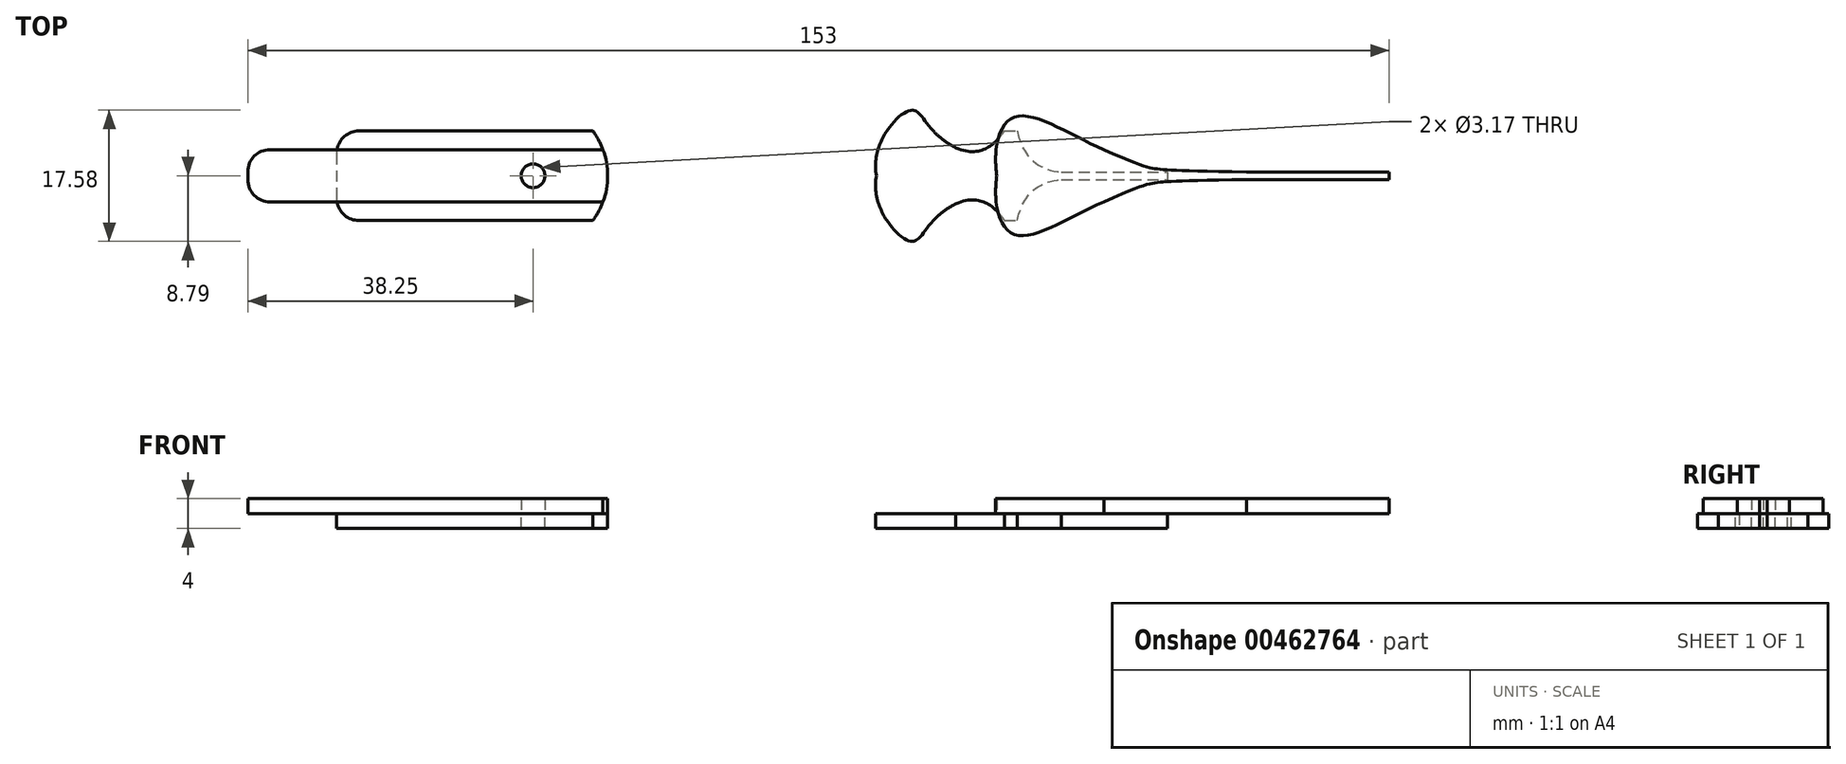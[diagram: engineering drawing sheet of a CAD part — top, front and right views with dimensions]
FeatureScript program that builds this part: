
annotation { "Feature Type Name" : "Feature", "Feature Type Description" : "" }
export const myFeature = defineFeature(function(context is Context, id is Id, definition is map)
    precondition{}
    {
        {
            var Q0;
            Q0=qCreatedBy(makeId("Top.planeOp"),FACE);
            var sketch = newSketch(context, id + "F0", { "sketchPlane" : qUnion([Q0])});
            skCircle(sketch, "E0", {"center": v(0, 0) * mm, "radius": 1.59 * mm});
            skLineSegment(sketch, "E1.bottom", {"start": v(-38.25, 3.5) * mm, "end": v(114.75, 3.5) * mm});
            skLineSegment(sketch, "E1.top", {"start": v(-38.25, -3.5) * mm, "end": v(114.75, -3.5) * mm});
            skLineSegment(sketch, "E1.left", {"start": v(-38.25, 3.5) * mm, "end": v(-38.25, -3.5) * mm});
            skLineSegment(sketch, "E1.right", {"start": v(114.75, 3.5) * mm, "end": v(114.75, -3.5) * mm});
            skCircle(sketch, "E2", {"center": v(0, 0) * mm, "radius": 10 * mm});
            skFitSpline(sketch, "E3", {"points": [v(76.5, -3.5) * mm, v(83.35, -0.96) * mm, v(95.63, -0.5) * mm], "startDerivative": vector(32.58, 14.52) * mm, "endDerivative": vector(48.68, 0.82) * mm});
            skFitSpline(sketch, "E4", {"points": [v(76.5, -3.5) * mm, v(64.47, -7.85) * mm, v(62.16, 0) * mm], "startDerivative": vector(-24.35, -10.45) * mm, "endDerivative": vector(3.38, 23.63) * mm});
            skLineSegment(sketch, "E5", {"start": v(0, 0) * mm, "end": v(229.5, 0) * mm, "construction": true});
            skLineSegment(sketch, "E6", {"start": v(95.63, -0.5) * mm, "end": v(114.75, -0.5) * mm});
            skFitSpline(sketch, "E7.MirrorCS", {"points": [v(76.5, 3.5) * mm, v(64.47, 7.85) * mm, v(62.16, 0) * mm], "startDerivative": vector(-24.35, 10.45) * mm, "endDerivative": vector(3.38, -23.63) * mm});
            skFitSpline(sketch, "E8.MirrorCS", {"points": [v(76.5, 3.5) * mm, v(83.35, 0.96) * mm, v(95.63, 0.5) * mm], "startDerivative": vector(32.58, -14.52) * mm, "endDerivative": vector(48.68, -0.82) * mm});
            skLineSegment(sketch, "E9.MirrorCS", {"start": v(95.63, 0.5) * mm, "end": v(114.75, 0.5) * mm});
            skSolve(sketch);
        }
        {
            var Q0;
            {var subQ0=sQuery(id+"F0.wireOp",EDGE,"E1.left");Q0=makeQuery(id+"F0.imprint","IMPRINT",FACE,{"disambiguationData":[TD([[makeQuery(id+"F0.imprint","IMPRINT",EDGE,{"derivedFrom":subQ0}),1.0]])]});}
            var Q1;
            {var subQ0=sQuery(id+"F0.wireOp",EDGE,"E2");var subQ1=sQuery(id+"F0.wireOp",EDGE,"E1.bottom");var subQ2=makeQuery(id+"F0.imprint","INTERSECT",VERTEX,{"disambiguationData":[OD(0.0)],"derivedFrom":[subQ1,subQ0]});Q1=makeQuery(id+"F0.imprint","IMPRINT",FACE,{"disambiguationData":[TD([[makeQuery(id+"F0.imprint","IMPRINT",EDGE,{"disambiguationData":[TD([[subQ2,-1.0]])],"derivedFrom":subQ1}),1.0]])]});}
            var Q2;
            {var subQ0=sQuery(id+"F0.wireOp",EDGE,"E7.MirrorCS");var subQ1=sQuery(id+"F0.wireOp",EDGE,"E1.bottom");var subQ3=makeQuery(id+"F0.imprint","INTERSECT",VERTEX,{"derivedFrom":[subQ1,subQ0]});Q2=makeQuery(id+"F0.imprint","IMPRINT",FACE,{"disambiguationData":[TD([[makeQuery(id+"F0.imprint","IMPRINT",EDGE,{"disambiguationData":[TD([[subQ3,-1.0]])],"derivedFrom":subQ1}),1.0]])]});}
            var Q3;
            {var subQ0=sQuery(id+"F0.wireOp",EDGE,"E2");var subQ1=sQuery(id+"F0.wireOp",EDGE,"E1.top");var subQ2=makeQuery(id+"F0.imprint","INTERSECT",VERTEX,{"disambiguationData":[OD(0.0)],"derivedFrom":[subQ1,subQ0]});Q3=makeQuery(id+"F0.imprint","IMPRINT",FACE,{"disambiguationData":[TD([[makeQuery(id+"F0.imprint","IMPRINT",EDGE,{"disambiguationData":[TD([[subQ2,-1.0]])],"derivedFrom":subQ1}),-1.0]])]});}
            var Q4;
            {var subQ0=sQuery(id+"F0.wireOp",EDGE,"E4");var subQ1=sQuery(id+"F0.wireOp",EDGE,"E1.top");var subQ3=makeQuery(id+"F0.imprint","INTERSECT",VERTEX,{"derivedFrom":[subQ1,subQ0]});Q4=makeQuery(id+"F0.imprint","IMPRINT",FACE,{"disambiguationData":[TD([[makeQuery(id+"F0.imprint","IMPRINT",EDGE,{"disambiguationData":[TD([[subQ3,-1.0]])],"derivedFrom":subQ1}),-1.0]])]});}
            var Q5;
            {var subQ5=sQuery(id+"F0.wireOp",EDGE,"E2");var subQ6=sQuery(id+"F0.wireOp",EDGE,"E1.bottom");var subQ7=makeQuery(id+"F0.imprint","INTERSECT",VERTEX,{"disambiguationData":[OD(1.0)],"derivedFrom":[subQ6,subQ5]});Q5=makeQuery(id+"F0.imprint","IMPRINT",FACE,{"disambiguationData":[TD([[makeQuery(id+"F0.imprint","IMPRINT",EDGE,{"disambiguationData":[TD([[subQ7,-1.0]])],"derivedFrom":subQ6}),-1.0]])]});}
            var Q6;
            Q6=makeQuery(id+"F0.imprint","IMPRINT",FACE,{"disambiguationData":[TD([[makeQuery(id+"F0.imprint","IMPRINT",EDGE,{"derivedFrom":sQuery(id+"F0.wireOp",EDGE,"E0")}),-1.0]])]});
            var Q7;
            {var subQ8=sQuery(id+"F0.wireOp",EDGE,"E3");Q7=makeQuery(id+"F0.imprint","IMPRINT",FACE,{"disambiguationData":[TD([[makeQuery(id+"F0.imprint","IMPRINT",EDGE,{"derivedFrom":subQ8}),1.0]])]});}
            extrude(context, id + "F1", {"entities" : qUnion([Q0, Q1, Q2, Q3, Q4, Q5, Q6, Q7]), "depth" : 2 * mm});
        }
        {
            var Q0;
            Q0=qCreatedBy(makeId("Top.planeOp"),FACE);
            var sketch = newSketch(context, id + "F2", { "sketchPlane" : qUnion([Q0])});
            skCircle(sketch, "E10", {"center": v(0, 0) * mm, "radius": 1.59 * mm});
            skLineSegment(sketch, "E11.bottom", {"start": v(-26.33, 6) * mm, "end": v(85, 6) * mm});
            skLineSegment(sketch, "E11.top", {"start": v(-26.33, -6) * mm, "end": v(85, -6) * mm});
            skLineSegment(sketch, "E11.left", {"start": v(-26.33, 6) * mm, "end": v(-26.33, -6) * mm});
            skLineSegment(sketch, "E11.right", {"start": v(85, 6) * mm, "end": v(85, -6) * mm});
            skCircle(sketch, "E12", {"center": v(0, 0) * mm, "radius": 10 * mm});
            skLineSegment(sketch, "E13.right", {"start": v(85, -12.54) * mm, "end": v(85, -19.22) * mm});
            skFitSpline(sketch, "E14", {"points": [v(56.67, -3.75) * mm, v(64.42, -7.88) * mm, v(70.83, -0.5) * mm], "startDerivative": vector(32.58, 14.52) * mm, "endDerivative": vector(38.81, 3.07) * mm});
            skFitSpline(sketch, "E15", {"points": [v(56.67, -3.75) * mm, v(50.67, -8.78) * mm, v(46.04, 0) * mm], "startDerivative": vector(-26.59, -13.5) * mm, "endDerivative": vector(5.2, 23.3) * mm});
            skLineSegment(sketch, "E16", {"start": v(0, 0) * mm, "end": v(229.5, 0) * mm, "construction": true});
            skLineSegment(sketch, "E17", {"start": v(70.83, -0.5) * mm, "end": v(85, -0.5) * mm});
            skFitSpline(sketch, "E18.MirrorCS", {"points": [v(56.67, 3.75) * mm, v(50.67, 8.78) * mm, v(46.04, 0) * mm], "startDerivative": vector(-26.59, 13.5) * mm, "endDerivative": vector(5.2, -23.3) * mm});
            skFitSpline(sketch, "E19.MirrorCS", {"points": [v(56.67, 3.75) * mm, v(64.42, 7.88) * mm, v(70.83, 0.5) * mm], "startDerivative": vector(32.58, -14.52) * mm, "endDerivative": vector(38.81, -3.07) * mm});
            skLineSegment(sketch, "E20.MirrorCS", {"start": v(70.83, 0.5) * mm, "end": v(85, 0.5) * mm});
            skSolve(sketch);
        }
        {
            var Q0;
            {var subQ0=sQuery(id+"F2.wireOp",EDGE,"E11.left");Q0=makeQuery(id+"F2.imprint","IMPRINT",FACE,{"disambiguationData":[TD([[makeQuery(id+"F2.imprint","IMPRINT",EDGE,{"derivedFrom":subQ0}),1.0]])]});}
            var Q1;
            {var subQ0=sQuery(id+"F2.wireOp",EDGE,"E12");var subQ1=sQuery(id+"F2.wireOp",EDGE,"E11.bottom");var subQ2=makeQuery(id+"F2.imprint","INTERSECT",VERTEX,{"disambiguationData":[OD(0.0)],"derivedFrom":[subQ1,subQ0]});Q1=makeQuery(id+"F2.imprint","IMPRINT",FACE,{"disambiguationData":[TD([[makeQuery(id+"F2.imprint","IMPRINT",EDGE,{"disambiguationData":[TD([[subQ2,-1.0]])],"derivedFrom":subQ1}),1.0]])]});}
            var Q2;
            {var subQ0=sQuery(id+"F2.wireOp",EDGE,"E12");var subQ1=sQuery(id+"F2.wireOp",EDGE,"E11.top");var subQ2=makeQuery(id+"F2.imprint","INTERSECT",VERTEX,{"disambiguationData":[OD(0.0)],"derivedFrom":[subQ1,subQ0]});Q2=makeQuery(id+"F2.imprint","IMPRINT",FACE,{"disambiguationData":[TD([[makeQuery(id+"F2.imprint","IMPRINT",EDGE,{"disambiguationData":[TD([[subQ2,-1.0]])],"derivedFrom":subQ1}),-1.0]])]});}
            var Q3;
            {var subQ0=sQuery(id+"F2.wireOp",EDGE,"E20.MirrorCS");var subQ1=sQuery(id+"F2.wireOp",EDGE,"E11.right");var subQ2=makeQuery(id+"F2.imprint","INTERSECT",VERTEX,{"derivedFrom":[subQ1,subQ0]});Q3=makeQuery(id+"F2.imprint","IMPRINT",FACE,{"disambiguationData":[TD([[makeQuery(id+"F2.imprint","IMPRINT",EDGE,{"disambiguationData":[TD([[subQ2,-1.0]])],"derivedFrom":subQ1}),1.0]])]});}
            var Q4;
            {var subQ5=sQuery(id+"F2.wireOp",EDGE,"E12");var subQ6=sQuery(id+"F2.wireOp",EDGE,"E11.bottom");var subQ7=makeQuery(id+"F2.imprint","INTERSECT",VERTEX,{"disambiguationData":[OD(1.0)],"derivedFrom":[subQ6,subQ5]});Q4=makeQuery(id+"F2.imprint","IMPRINT",FACE,{"disambiguationData":[TD([[makeQuery(id+"F2.imprint","IMPRINT",EDGE,{"disambiguationData":[TD([[subQ7,-1.0]])],"derivedFrom":subQ6}),-1.0]])]});}
            var Q5;
            Q5=makeQuery(id+"F2.imprint","IMPRINT",FACE,{"disambiguationData":[TD([[makeQuery(id+"F2.imprint","IMPRINT",EDGE,{"derivedFrom":sQuery(id+"F2.wireOp",EDGE,"E10")}),-1.0]])]});
            var Q6;
            {var subQ0=sQuery(id+"F2.wireOp",EDGE,"E17");Q6=makeQuery(id+"F2.imprint","IMPRINT",FACE,{"disambiguationData":[TD([[makeQuery(id+"F2.imprint","IMPRINT",EDGE,{"derivedFrom":subQ0}),1.0]])]});}
            var Q7;
            {var subQ0=sQuery(id+"F2.wireOp",EDGE,"E14");var subQ1=sQuery(id+"F2.wireOp",EDGE,"E11.top");var subQ2=makeQuery(id+"F2.imprint","INTERSECT",VERTEX,{"disambiguationData":[OD(0.0)],"derivedFrom":[subQ1,subQ0]});Q7=makeQuery(id+"F2.imprint","IMPRINT",FACE,{"disambiguationData":[TD([[makeQuery(id+"F2.imprint","IMPRINT",EDGE,{"disambiguationData":[TD([[subQ2,-1.0]])],"derivedFrom":subQ1}),-1.0]])]});}
            var Q8;
            {var subQ0=sQuery(id+"F2.wireOp",EDGE,"E19.MirrorCS");var subQ1=sQuery(id+"F2.wireOp",EDGE,"E11.bottom");var subQ2=makeQuery(id+"F2.imprint","INTERSECT",VERTEX,{"disambiguationData":[OD(0.0)],"derivedFrom":[subQ1,subQ0]});Q8=makeQuery(id+"F2.imprint","IMPRINT",FACE,{"disambiguationData":[TD([[makeQuery(id+"F2.imprint","IMPRINT",EDGE,{"disambiguationData":[TD([[subQ2,-1.0]])],"derivedFrom":subQ1}),1.0]])]});}
            var Q9;
            {var subQ0=sQuery(id+"F2.wireOp",EDGE,"E18.MirrorCS");var subQ1=sQuery(id+"F2.wireOp",EDGE,"E11.bottom");var subQ2=makeQuery(id+"F2.imprint","INTERSECT",VERTEX,{"disambiguationData":[OD(0.0)],"derivedFrom":[subQ1,subQ0]});Q9=makeQuery(id+"F2.imprint","IMPRINT",FACE,{"disambiguationData":[TD([[makeQuery(id+"F2.imprint","IMPRINT",EDGE,{"disambiguationData":[TD([[subQ2,-1.0]])],"derivedFrom":subQ1}),1.0]])]});}
            var Q10;
            {var subQ0=sQuery(id+"F2.wireOp",EDGE,"E15");var subQ1=sQuery(id+"F2.wireOp",EDGE,"E11.top");var subQ2=makeQuery(id+"F2.imprint","INTERSECT",VERTEX,{"disambiguationData":[OD(0.0)],"derivedFrom":[subQ1,subQ0]});Q10=makeQuery(id+"F2.imprint","IMPRINT",FACE,{"disambiguationData":[TD([[makeQuery(id+"F2.imprint","IMPRINT",EDGE,{"disambiguationData":[TD([[subQ2,-1.0]])],"derivedFrom":subQ1}),-1.0]])]});}
            extrude(context, id + "F3", {"entities" : qUnion([Q0, Q1, Q2, Q3, Q4, Q5, Q6, Q7, Q8, Q9, Q10]), "oppositeDirection" : true, "depth" : 2 * mm});
        }
        {
            var Q0;
            Q0=makeQuery(id+"F3.opExtrude","SWEPT_EDGE",EDGE,{"disambiguationData":[OSD([sQuery(id+"F2.wireOp",EDGE,"E11.bottom"),sQuery(id+"F2.wireOp",EDGE,"E11.left")])]});
            var Q1;
            Q1=makeQuery(id+"F3.opExtrude","SWEPT_EDGE",EDGE,{"disambiguationData":[OSD([sQuery(id+"F2.wireOp",EDGE,"E11.top"),sQuery(id+"F2.wireOp",EDGE,"E11.left")])]});
            var Q2;
            Q2=makeQuery(id+"F1.opExtrude","SWEPT_EDGE",EDGE,{"disambiguationData":[OSD([sQuery(id+"F0.wireOp",EDGE,"E1.bottom"),sQuery(id+"F0.wireOp",EDGE,"E1.left")])]});
            var Q3;
            Q3=makeQuery(id+"F1.opExtrude","SWEPT_EDGE",EDGE,{"disambiguationData":[OSD([sQuery(id+"F0.wireOp",EDGE,"E1.top"),sQuery(id+"F0.wireOp",EDGE,"E1.left")])]});
            fillet(context, id + "F4", {"entities" : qUnion([Q0, Q1, Q2, Q3]), "radius" : 3 * mm, "tangentPropagation" : true, "allowEdgeOverflow" : false});
        }
    });
